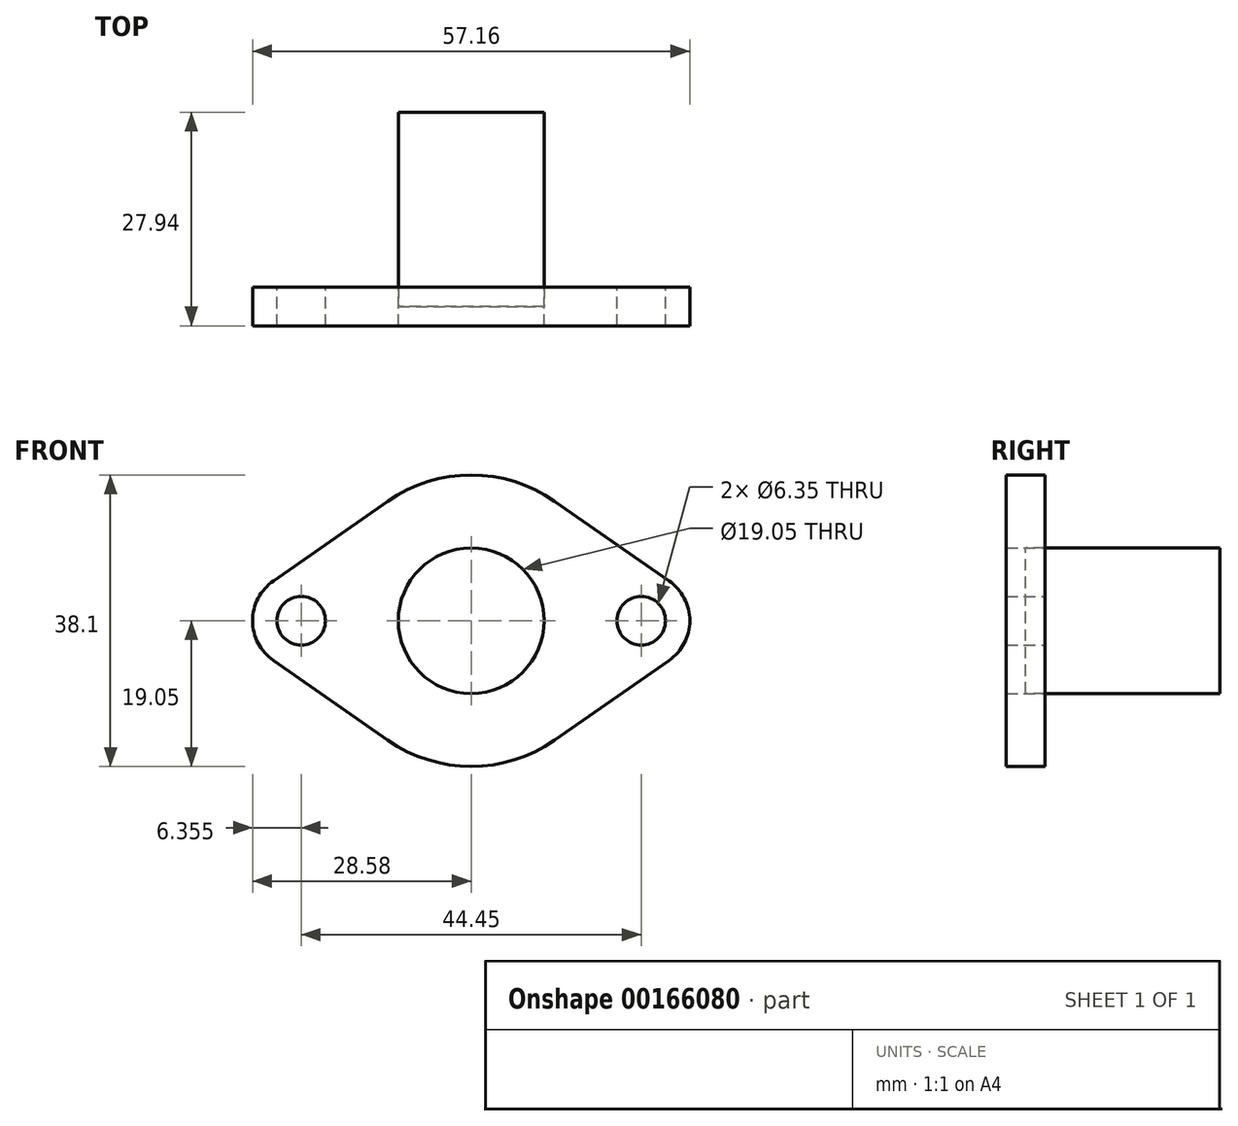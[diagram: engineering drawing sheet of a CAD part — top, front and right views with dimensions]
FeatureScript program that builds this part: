
annotation { "Feature Type Name" : "Feature", "Feature Type Description" : "" }
export const myFeature = defineFeature(function(context is Context, id is Id, definition is map)
    precondition{}
    {
        {
            var Q0;
            Q0=qCreatedBy(makeId("Front.planeOp"),FACE);
            var sketch = newSketch(context, id + "F0", { "sketchPlane" : qUnion([Q0])});
            skCircle(sketch, "E0", {"center": v(0, 0) * mm, "radius": 9.53 * mm});
            skArc(sketch, "E1", {"start": v(-10.89, -15.63) * mm, "mid": v(0, -19.05) * mm, "end": v(10.89, -15.63) * mm});
            skCircle(sketch, "E2", {"center": v(22.23, 0) * mm, "radius": 3.18 * mm});
            skArc(sketch, "E3", {"start": v(25.85, -5.21) * mm, "mid": v(28.58, 0) * mm, "end": v(25.85, 5.21) * mm});
            skCircle(sketch, "E4", {"center": v(-22.23, 0) * mm, "radius": 3.18 * mm});
            skArc(sketch, "E5", {"start": v(-25.85, 5.21) * mm, "mid": v(-28.58, 0) * mm, "end": v(-25.85, -5.21) * mm});
            skArc(sketch, "E6.trimOffspring", {"start": v(10.89, 15.63) * mm, "mid": v(0, 19.05) * mm, "end": v(-10.89, 15.63) * mm});
            skLineSegment(sketch, "E7", {"start": v(-25.85, 5.21) * mm, "end": v(-10.89, 15.63) * mm});
            skLineSegment(sketch, "E8", {"start": v(25.85, 5.21) * mm, "end": v(10.89, 15.63) * mm});
            skLineSegment(sketch, "E9", {"start": v(10.89, -15.63) * mm, "end": v(25.85, -5.21) * mm});
            skLineSegment(sketch, "E10", {"start": v(-10.89, -15.63) * mm, "end": v(-25.85, -5.21) * mm});
            skSolve(sketch);
        }
        {
            var Q0;
            Q0=makeQuery(id+"F0.imprint","IMPRINT",FACE,{"disambiguationData":[TD([[makeQuery(id+"F0.imprint","IMPRINT",EDGE,{"derivedFrom":sQuery(id+"F0.wireOp",EDGE,"E0")}),-1.0]])]});
            extrude(context, id + "F1", {"entities" : qUnion([Q0]), "endBound" : BoundingType.SYMMETRIC, "depth" : 5.08 * mm});
        }
        {
            var Q0;
            Q0=makeQuery(id+"F0.imprint","IMPRINT",FACE,{"disambiguationData":[TD([[makeQuery(id+"F0.imprint","IMPRINT",EDGE,{"derivedFrom":sQuery(id+"F0.wireOp",EDGE,"E0")}),1.0]])]});
            var Q1;
            Q1=sQuery(id+"F0.wireOp",EDGE,"E0");
            extrude(context, id + "F2", {"entities" : qUnion([Q0]), "surfaceEntities" : qUnion([Q1]), "oppositeDirection" : true, "depth" : 25.4 * mm});
        }
        {
            var Q0;
            Q0=sQuery(id+"F0.wireOp",VERTEX,"E0.center");
            var Q1;
            Q1=makeQuery(id+"F1.opExtrude","SWEPT_BODY",BODY,{"disambiguationData":[OSD([sQuery(id+"F0.wireOp",EDGE,"E0"),sQuery(id+"F0.wireOp",EDGE,"E1"),sQuery(id+"F0.wireOp",EDGE,"E2"),sQuery(id+"F0.wireOp",EDGE,"E3"),sQuery(id+"F0.wireOp",EDGE,"E4"),sQuery(id+"F0.wireOp",EDGE,"E5"),sQuery(id+"F0.wireOp",EDGE,"E6.trimOffspring"),sQuery(id+"F0.wireOp",EDGE,"E7"),sQuery(id+"F0.wireOp",EDGE,"E8"),sQuery(id+"F0.wireOp",EDGE,"E9"),sQuery(id+"F0.wireOp",EDGE,"E10")])]});
            hole(context, id + "F3", {"style" : HoleStyle.SIMPLE, "endStyle" : HoleEndStyle.THROUGH, "holeDiameter" : 17.78 * mm, "locations" : qUnion([Q0]), "scope" : qUnion([Q1]), "isTappedThrough" : true});
        }
    });
